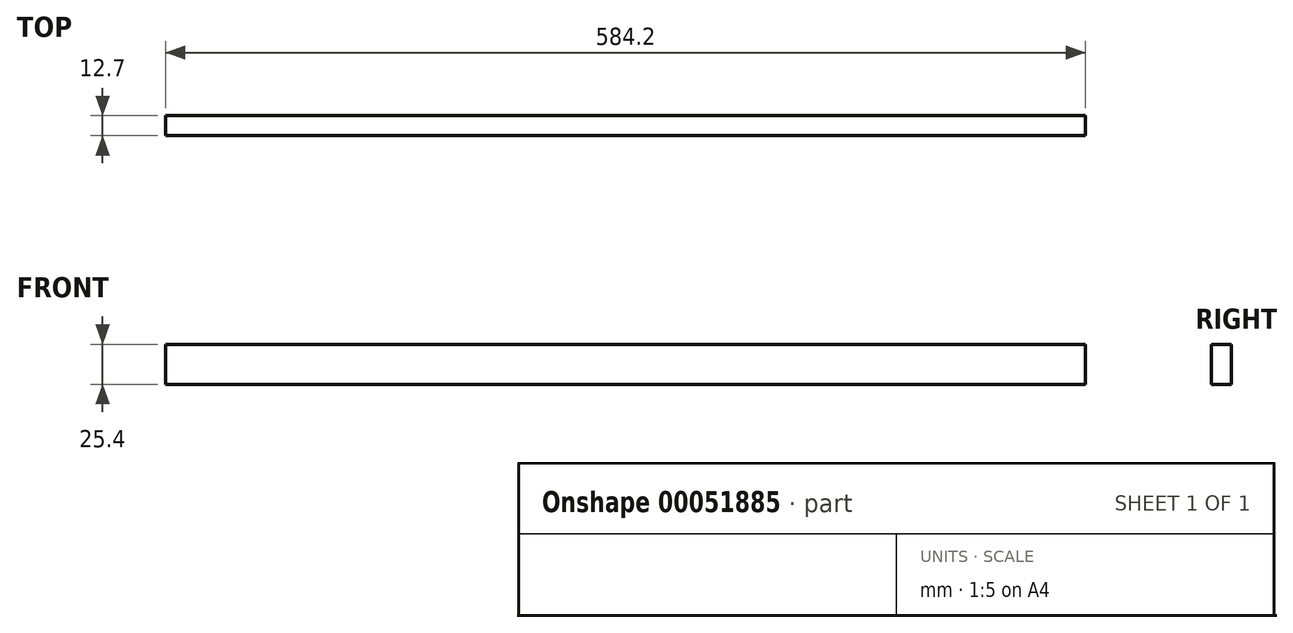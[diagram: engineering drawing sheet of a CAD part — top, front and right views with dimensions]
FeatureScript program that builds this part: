
annotation { "Feature Type Name" : "Feature", "Feature Type Description" : "" }
export const myFeature = defineFeature(function(context is Context, id is Id, definition is map)
    precondition{}
    {
        {
            var Q0;
            Q0=qCreatedBy(makeId("Front.planeOp"),FACE);
            var sketch = newSketch(context, id + "F0", { "sketchPlane" : qUnion([Q0])});
            skLineSegment(sketch, "E0.bottom", {"start": v(-292.1, 0) * mm, "end": v(292.1, 0) * mm});
            skLineSegment(sketch, "E0.top", {"start": v(-292.1, 25.4) * mm, "end": v(292.1, 25.4) * mm});
            skLineSegment(sketch, "E0.left", {"start": v(-292.1, 0) * mm, "end": v(-292.1, 25.4) * mm});
            skLineSegment(sketch, "E0.right", {"start": v(292.1, 0) * mm, "end": v(292.1, 25.4) * mm});
            skSolve(sketch);
        }
        {
            var Q0;
            Q0=makeQuery(id+"F0.imprint","IMPRINT",FACE,{"disambiguationData":[TD([[makeQuery(id+"F0.imprint","IMPRINT",EDGE,{"derivedFrom":sQuery(id+"F0.wireOp",EDGE,"E0.bottom")}),1.0]])]});
            extrude(context, id + "F1", {"entities" : qUnion([Q0]), "depth" : 12.7 * mm});
        }
    });
